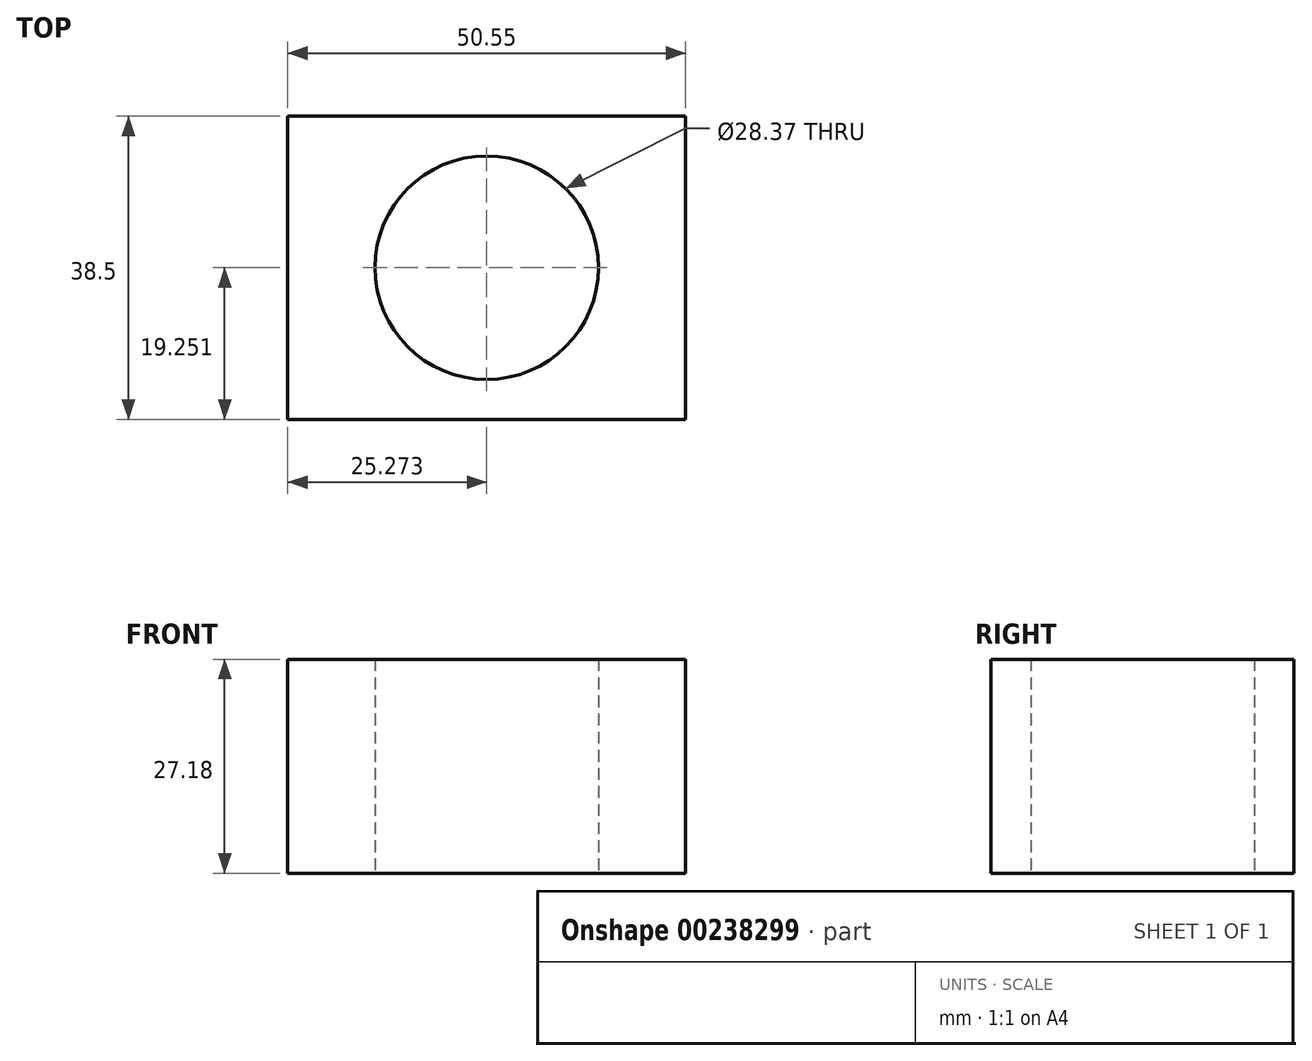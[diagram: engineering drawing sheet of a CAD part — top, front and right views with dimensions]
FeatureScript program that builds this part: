
annotation { "Feature Type Name" : "Feature", "Feature Type Description" : "" }
export const myFeature = defineFeature(function(context is Context, id is Id, definition is map)
    precondition{}
    {
        {
            var Q0;
            Q0=qCreatedBy(makeId("Top.planeOp"),FACE);
            var sketch = newSketch(context, id + "F0", { "sketchPlane" : qUnion([Q0])});
            skLineSegment(sketch, "E0.bottom", {"start": v(0, 0) * mm, "end": v(50.55, 0) * mm});
            skLineSegment(sketch, "E0.top", {"start": v(0, 38.5) * mm, "end": v(50.55, 38.5) * mm});
            skLineSegment(sketch, "E0.left", {"start": v(0, 0) * mm, "end": v(0, 38.5) * mm});
            skLineSegment(sketch, "E0.right", {"start": v(50.55, 0) * mm, "end": v(50.55, 38.5) * mm});
            skSolve(sketch);
        }
        {
            var Q0;
            Q0=makeQuery(id+"F0.imprint","IMPRINT",FACE,{"disambiguationData":[TD([[makeQuery(id+"F0.imprint","IMPRINT",EDGE,{"derivedFrom":sQuery(id+"F0.wireOp",EDGE,"E0.bottom")}),1.0]])]});
            extrude(context, id + "F1", {"entities" : qUnion([Q0]), "depth" : 27.18 * mm});
        }
        {
            var Q0;
            Q0=makeQuery(id+"F1.opExtrude","CAP_FACE",FACE,{"disambiguationData":[OSD([sQuery(id+"F0.wireOp",EDGE,"E0.bottom"),sQuery(id+"F0.wireOp",EDGE,"E0.top"),sQuery(id+"F0.wireOp",EDGE,"E0.left"),sQuery(id+"F0.wireOp",EDGE,"E0.right")])],"isStart":true});
            var sketch = newSketch(context, id + "F2", { "sketchPlane" : qUnion([Q0])});
            skCircle(sketch, "E1", {"center": v(25.27, -19.25) * mm, "radius": 14.19 * mm});
            skPoint(sketch, "E1.centerSnap0", {"position": v(0, -19.25) * mm});
            skPoint(sketch, "E1.centerSnap1", {"position": v(25.27, 0) * mm});
            skSolve(sketch);
        }
        {
            var Q0;
            Q0 = qSketchRegion(id + "F2", true);
            extrude(context, id + "F3", {"entities" : qUnion([Q0]), "operationType" : NewBodyOperationType.REMOVE, "endBound" : BoundingType.THROUGH_ALL, "oppositeDirection" : true, "depth" : 15.24 * mm});
        }
    });
